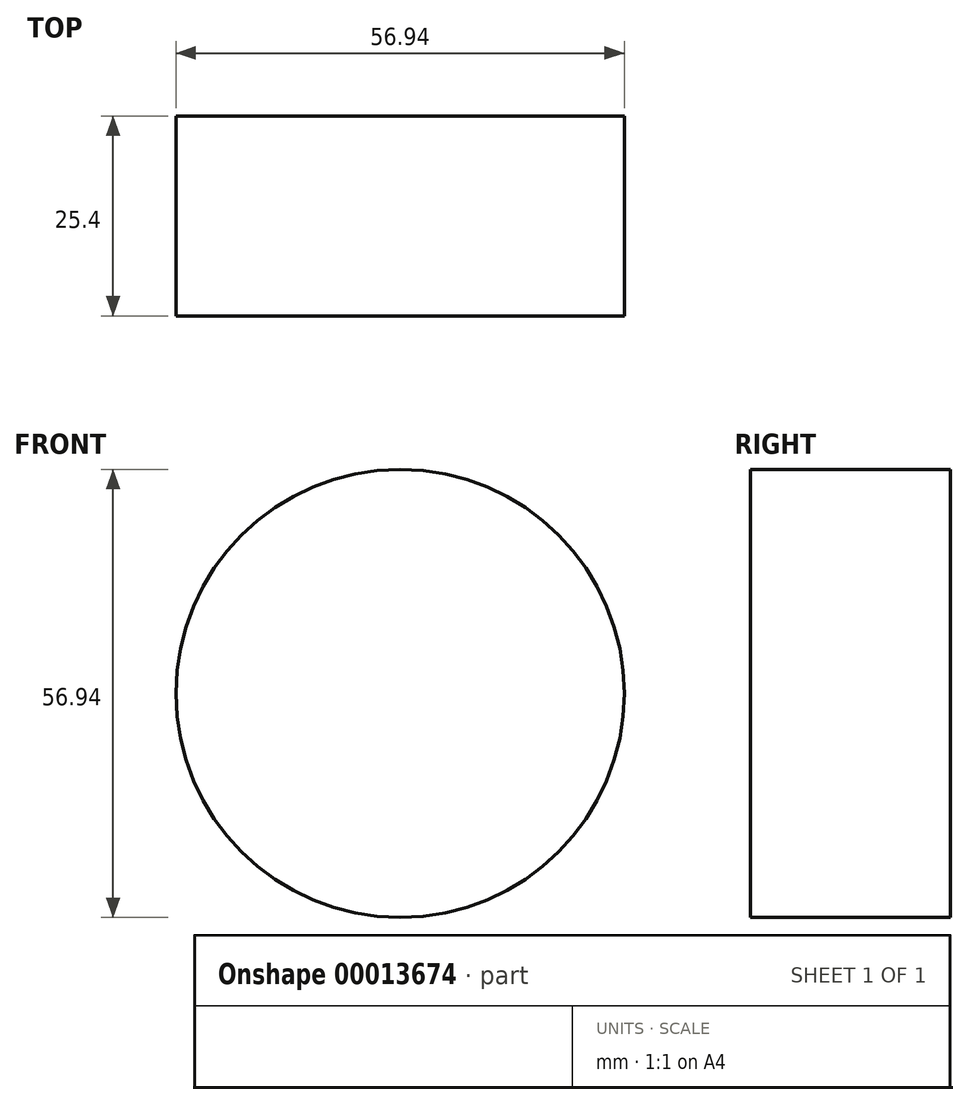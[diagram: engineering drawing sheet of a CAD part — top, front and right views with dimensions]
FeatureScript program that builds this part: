
annotation { "Feature Type Name" : "Feature", "Feature Type Description" : "" }
export const myFeature = defineFeature(function(context is Context, id is Id, definition is map)
    precondition{}
    {
        {
            var Q0;
            Q0=qCreatedBy(makeId("Front.planeOp"),FACE);
            var sketch = newSketch(context, id + "F0", { "sketchPlane" : qUnion([Q0])});
            skCircle(sketch, "E0", {"center": v(0, 0) * mm, "radius": 28.47 * mm});
            skSolve(sketch);
        }
        {
            var Q0;
            Q0=makeQuery(id+"F0.imprint","IMPRINT",FACE,{"disambiguationData":[TD([[makeQuery(id+"F0.imprint","IMPRINT",EDGE,{"derivedFrom":sQuery(id+"F0.wireOp",EDGE,"E0")}),1.0]])]});
            extrude(context, id + "F1", {"entities" : qUnion([Q0]), "depth" : 25.4 * mm});
        }
    });
